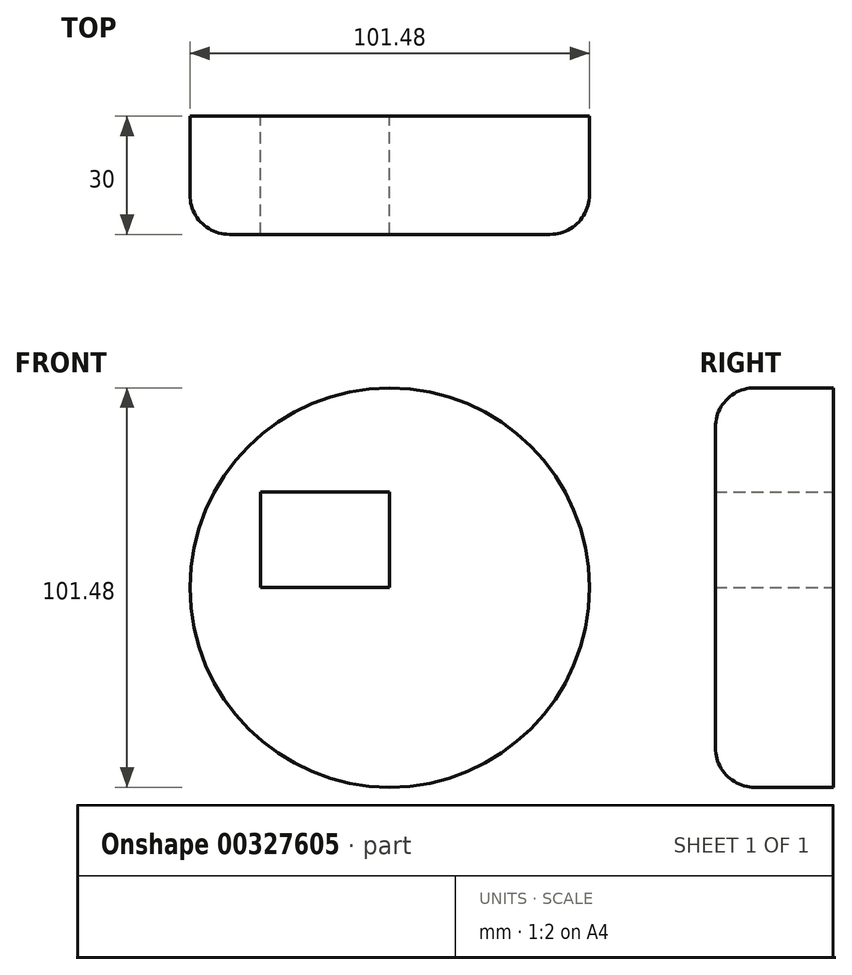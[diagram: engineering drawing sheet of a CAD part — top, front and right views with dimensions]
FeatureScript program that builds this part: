
annotation { "Feature Type Name" : "Feature", "Feature Type Description" : "" }
export const myFeature = defineFeature(function(context is Context, id is Id, definition is map)
    precondition{}
    {
        {
            var Q0;
            Q0=qCreatedBy(makeId("Front.planeOp"),FACE);
            var sketch = newSketch(context, id + "F0", { "sketchPlane" : qUnion([Q0])});
            skCircle(sketch, "E0", {"center": v(0, 0) * mm, "radius": 50.74 * mm});
            skSolve(sketch);
        }
        {
            var Q0;
            Q0=makeQuery(id+"F0.imprint","IMPRINT",FACE,{"disambiguationData":[TD([[makeQuery(id+"F0.imprint","IMPRINT",EDGE,{"derivedFrom":sQuery(id+"F0.wireOp",EDGE,"E0")}),1.0]])]});
            extrude(context, id + "F1", {"entities" : qUnion([Q0]), "depth" : 30 * mm});
        }
        {
            var Q0;
            Q0=makeQuery(id+"F1.opExtrude","CAP_FACE",FACE,{"disambiguationData":[OSD([sQuery(id+"F0.wireOp",EDGE,"E0")])],"isStart":true});
            var sketch = newSketch(context, id + "F2", { "sketchPlane" : qUnion([Q0])});
            skLineSegment(sketch, "E1.bottom", {"start": v(0, 0) * mm, "end": v(32.75, 0) * mm});
            skLineSegment(sketch, "E1.top", {"start": v(0, 24.25) * mm, "end": v(32.75, 24.25) * mm});
            skLineSegment(sketch, "E1.left", {"start": v(0, 0) * mm, "end": v(0, 24.25) * mm});
            skLineSegment(sketch, "E1.right", {"start": v(32.75, 0) * mm, "end": v(32.75, 24.25) * mm});
            skSolve(sketch);
        }
        {
            var Q0;
            Q0 = qSketchRegion(id + "F2", true);
            extrude(context, id + "F3", {"entities" : qUnion([Q0]), "operationType" : NewBodyOperationType.REMOVE, "oppositeDirection" : true, "depth" : 96.84 * mm});
        }
        {
            var Q0;
            Q0=makeQuery(id+"F1.opExtrude","CAP_EDGE",EDGE,{"disambiguationData":[OSD([sQuery(id+"F0.wireOp",EDGE,"E0")])],"isStart":false});
            fillet(context, id + "F4", {"entities" : qUnion([Q0]), "radius" : 10 * mm, "tangentPropagation" : true, "allowEdgeOverflow" : false});
        }
    });
